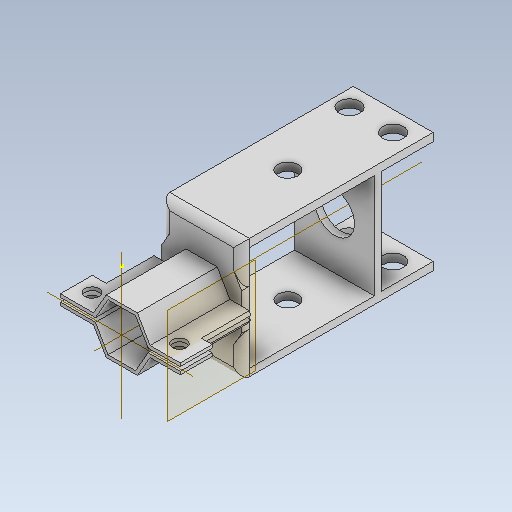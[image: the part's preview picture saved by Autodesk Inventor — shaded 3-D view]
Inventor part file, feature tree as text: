
AUTODESK INVENTOR PART (.ipt)
format: ipt  version: 2021 (Build 250183000, 183)  size: 421,888 bytes
history: native  units: mm
features: sketch x17, extrude x15, other x6, move_body x6, mirror x5, projected_geometry x4, direct_edit x3, reference x2, plane x1, fillet x1
ambient origin geometry x8: Origin, YZ Plane, XZ Plane, XY Plane, X Axis, Y Axis, Z Axis, Center Point
bodies: Solid1 (feature_tree)
feature tree (60):
  extrude  "Extrusion1"  Depth=5.0mm
  extrude  "Extrusion3"  Depth=6.9mm
  extrude  "Extrusion4"  Depth=10.0mm
  extrude  "Extrusion5"  Depth=1.0mm
  plane  "Work Plane1"
  extrude  "Extrusion6"  Depth=0.8mm
  mirror  "Mirror1"
  mirror  "Mirror2"
  extrude  "Extrusion7"  Depth=8.0mm TaperAngle=0.0deg
  mirror  "Mirror3"
  extrude  "Extrusion8"  Depth=5.0mm TaperAngle=0.0deg
  fillet  "Fillet1"  Radius=20.0mm
  extrude  "Extrusion9"  Depth=35.0mm TaperAngle=0.0deg
  extrude  "Extrusion10"  Depth=5.0mm
  sketch  "Sketch12"  dims[d31=35.0mm d32=0.0mm d33=3.0mm]
  sketch  "Sketch14"  dims[d34=3.0mm d35=10.0mm d36=0.0mm]
  extrude  "Extrusion13"  Depth=35.0mm
  extrude  "Extrusion14"  Depth=10.0mm TaperAngle=0.0deg
  extrude  "Extrusion15"  Depth=33.0mm TaperAngle=0.0deg
  mirror  "Mirror4"
  extrude  "Extrusion16"  Depth=20.0mm
  extrude  "Extrusion17"  TaperAngle=0.0deg  [1 undecoded]
  extrude  "Extrusion18"  Depth=1.0mm TaperAngle=0.0deg
  mirror  "Mirror5"
  direct_edit  "Direct Edit1"
  direct_edit  "Direct Edit2"
  direct_edit  "Direct Edit3"
  sketch  "Sketch1"  dims[d0=6.9mm d1=5.0mm]
  sketch  "Sketch4"  dims[d2=20.0mm d3=0.0mm d7=6.9mm]
  sketch  "Sketch5"  dims[d8=10.0mm d9=0.0mm d10=10.0mm]
  sketch  "Sketch6"  dims[d11=10.0mm d12=0.0mm d13=1.0mm]
  sketch  "Sketch7"  dims[d14=10.0mm d15=0.0mm d16=0.8mm]
  sketch  "Sketch8"  dims[d17=8.0mm d18=8.0mm d19=1.0mm d20=0.0mm d21=0.0mm]
  sketch  "Sketch9"  dims[d22=3.5mm d23=5.0mm d24=0.0mm d25=20.0mm]
  sketch  "Sketch10"  dims[d26=30.0mm d27=35.0mm d28=0.0mm]
  sketch  "Sketch11"  dims[d29=2.0mm d30=5.0mm]
  sketch  "Sketch16"  dims[d43=33.0mm d44=0.0mm d45=3.0mm d46=0.0mm]
  reference  "Reference2"
  reference  "Reference3"
  sketch  "Sketch17"  dims[d47=20.0mm d48=0.0mm d49=3.5mm]
  projected_geometry  "Projected Loop1"
  projected_geometry  "Projected Loop2"
  sketch  "Sketch18"  dims[d50=10.0mm d51=0.0mm d52=0.0mm d53=0.0mm]
  projected_geometry  "Projected Loop3"
  sketch  "Sketch19"  dims[d54=42.25mm d55=0.0mm d56=0.0mm d57=0.0mm d58=1.0mm]
  sketch  "Sketch20"  dims[d59=0.0mm d60=0.0mm d61=-1.0mm]
  sketch  "Sketch21"  dims[d62=0.0mm d63=0.0mm d64=-1.0mm d65=0.0mm d66=0.0mm d67=-1.0mm d68=-1.0mm d69=0.0mm d70=0.0mm d71=-5.75mm d72=0.0mm d73=0.0mm d74=-5.0mm d75=-1.0mm]
  projected_geometry  "Projected Loop4"
  parser-record x1  (decoder bookkeeping rows leaked as tree rows — omitted from the tree; the rows remain in map.json)
  other  "whole_assembly.iam"
  other  "Part3:1"
  other  "tool_holder:1"
  move_body  "Move1"
  move_body  "Move2"
  move_body  "Move3"
  move_body  "Move4"
  other  "Size1"
  move_body  "Move5"
  move_body  "Move6"
  other  "Size2"
note: 1 required parameter value undecoded (feature->parameter linkage not recoverable at this tier; creation-order binding heuristic only, values carry confidence <= 0.55)
note: 1 file-system path scrubbed to <path> (originals preserved in map.json)
